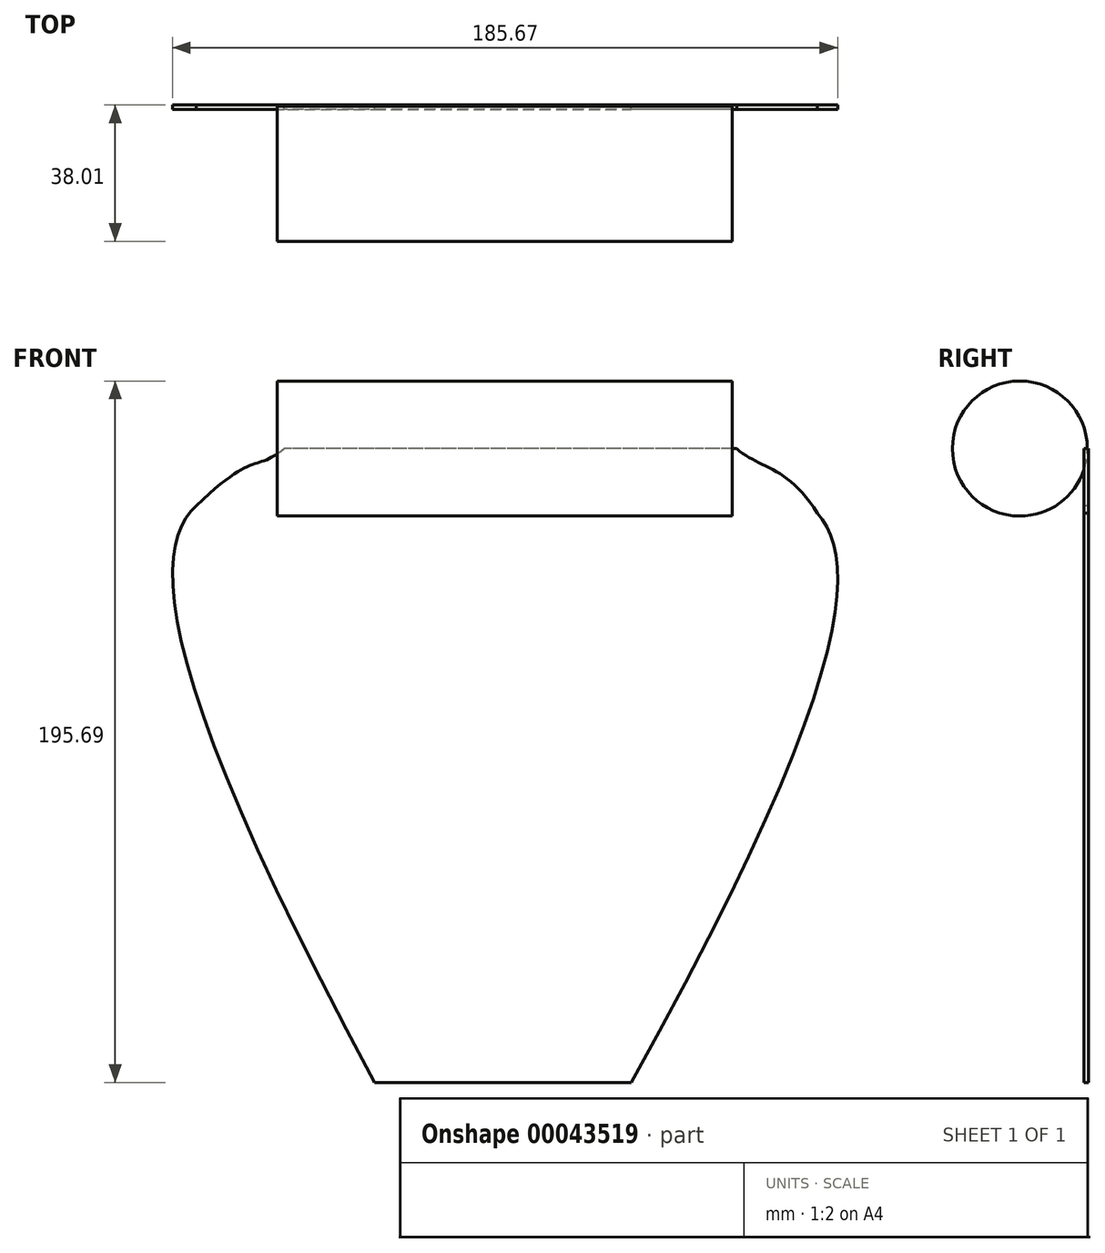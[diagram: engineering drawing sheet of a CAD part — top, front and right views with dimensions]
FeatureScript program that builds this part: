
annotation { "Feature Type Name" : "Feature", "Feature Type Description" : "" }
export const myFeature = defineFeature(function(context is Context, id is Id, definition is map)
    precondition{}
    {
        {
            var Q0;
            Q0=qCreatedBy(makeId("Right.planeOp"),FACE);
            var sketch = newSketch(context, id + "F0", { "sketchPlane" : qUnion([Q0])});
            skCircle(sketch, "E0", {"center": v(-19.17, 0) * mm, "radius": 18.84 * mm});
            skSolve(sketch);
        }
        {
            var Q0;
            Q0 = qSketchRegion(id + "F0", true);
            extrude(context, id + "F1", {"entities" : qUnion([Q0]), "oppositeDirection" : true, "depth" : 63.5 * mm});
        }
        {
            var Q0;
            Q0=makeQuery(id+"F1.opExtrude","CAP_FACE",FACE,{"disambiguationData":[OSD([sQuery(id+"F0.wireOp",EDGE,"E0")])],"isStart":true});
            extrude(context, id + "F2", {"entities" : qUnion([Q0]), "operationType" : NewBodyOperationType.ADD, "depth" : 63.5 * mm});
        }
        {
            var Q0;
            Q0=qCreatedBy(makeId("Front.planeOp"),FACE);
            var sketch = newSketch(context, id + "F3", { "sketchPlane" : qUnion([Q0])});
            skFitSpline(sketch, "E1", {"points": [v(-61.56, 0) * mm, v(-36.26, -176.85) * mm], "startDerivative": vector(3.65, -76.9) * mm, "endDerivative": vector(332.33, -614.42) * mm});
            skFitSpline(sketch, "E2", {"points": [v(64.75, 0) * mm, v(35.39, -176.85) * mm], "startDerivative": vector(0.23, -75.85) * mm, "endDerivative": vector(-327.99, -588.12) * mm});
            skLineSegment(sketch, "E3", {"start": v(-36.26, -176.85) * mm, "end": v(35.39, -176.85) * mm});
            skLineSegment(sketch, "E4", {"start": v(64.75, 0) * mm, "end": v(-61.56, 0) * mm});
            skFitSpline(sketch, "E5", {"points": [v(87.29, -18.08) * mm, v(64.75, 0) * mm], "startDerivative": vector(-24.25, 40.19) * mm, "endDerivative": vector(-18.73, 17.01) * mm});
            skFitSpline(sketch, "E6", {"points": [v(-86.06, -15.96) * mm, v(-61.56, 0) * mm], "startDerivative": vector(49.75, 47.87) * mm, "endDerivative": vector(24.7, 20.55) * mm});
            skSolve(sketch);
        }
        {
            var Q0;
            Q0 = qSketchRegion(id + "F3", true);
            extrude(context, id + "F4", {"entities" : qUnion([Q0]), "depth" : 1.27 * mm});
        }
    });
